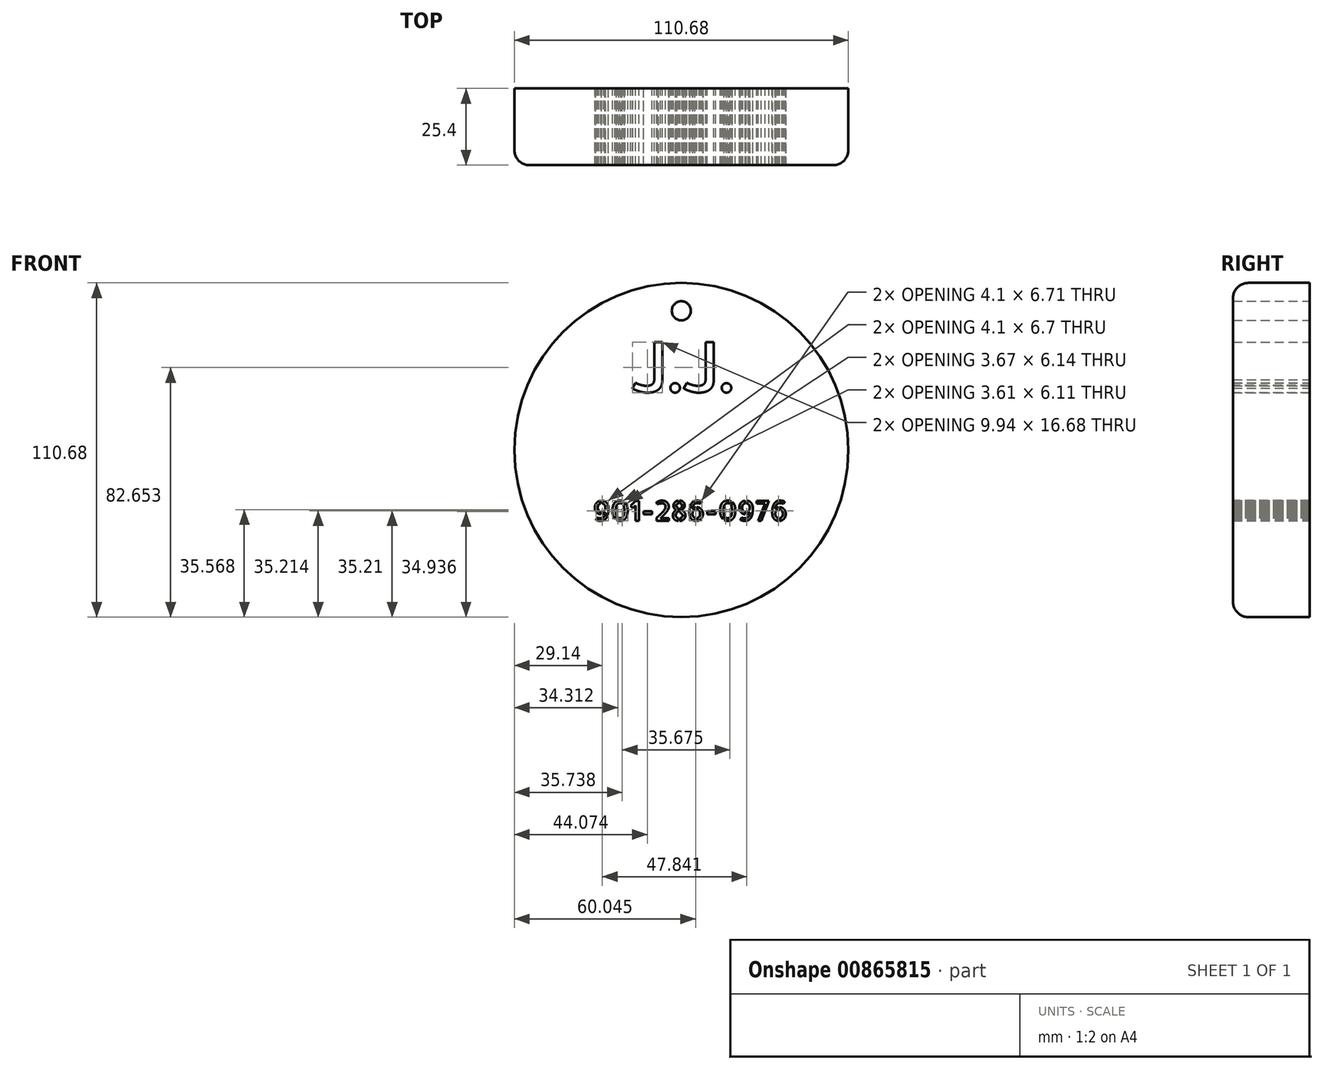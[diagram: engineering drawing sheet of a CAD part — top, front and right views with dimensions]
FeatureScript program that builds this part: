
annotation { "Feature Type Name" : "Feature", "Feature Type Description" : "" }
export const myFeature = defineFeature(function(context is Context, id is Id, definition is map)
    precondition{}
    {
        {
            var Q0;
            Q0=qCreatedBy(makeId("Front.planeOp"),FACE);
            var sketch = newSketch(context, id + "F0", { "sketchPlane" : qUnion([Q0])});
            skCircle(sketch, "E0", {"center": v(0, 0) * mm, "radius": 55.34 * mm});
            skText(sketch, "E1", { "text": "J.J.", "fontName": "AllertaStencil-Regular.ttf"});
            skText(sketch, "E2", { "text": "901-286-0976", "fontName": "AllertaStencil-Regular.ttf"});
            const initialGuessF0  = {"E1": [-0.01681, 0.01908, 1, 0, 0.01625], "E2": [-0.02928, -0.02343, 1, 0, 0.00661]};
            skSetInitialGuess(sketch, initialGuessF0);
            skSolve(sketch);
        }
        {
            var Q0;
            Q0 = qSketchRegion(id + "F0", true);
            var Q1;
            Q1=makeQuery(id+"F0.imprint","IMPRINT",FACE,{"disambiguationData":[TD([[makeQuery(id+"F0.imprint","IMPRINT",EDGE,{"derivedFrom":sQuery(id+"F0.wireOp",EDGE,"E0")}),1.0]])]});
            extrude(context, id + "F1", {"entities" : qUnion([Q0, Q1]), "depth" : 25.4 * mm, "offsetDistance" : 25.4 * mm});
        }
        {
            var Q0;
            Q0=qCreatedBy(makeId("Front.planeOp"),FACE);
            var sketch = newSketch(context, id + "F2", { "sketchPlane" : qUnion([Q0])});
            skPoint(sketch, "E3", {"position": v(0, 46.1) * mm});
            skSolve(sketch);
        }
        {
            var Q0;
            Q0=sQuery(id+"F2.wireOp",VERTEX,"E3");
            var Q1;
            Q1=makeQuery(id+"F1.opExtrude","SWEPT_BODY",BODY,{"disambiguationData":[OSD([sQuery(id+"F0.wireOp",EDGE,"E0"),sQuery(id+"F0.wireOp",EDGE,"E1.sketch_text.stroke-0"),sQuery(id+"F0.wireOp",EDGE,"E1.sketch_text.stroke-1"),sQuery(id+"F0.wireOp",EDGE,"E1.sketch_text.stroke-2"),sQuery(id+"F0.wireOp",EDGE,"E1.sketch_text.stroke-3"),sQuery(id+"F0.wireOp",EDGE,"E1.sketch_text.stroke-4"),sQuery(id+"F0.wireOp",EDGE,"E1.sketch_text.stroke-5"),sQuery(id+"F0.wireOp",EDGE,"E1.sketch_text.stroke-6"),sQuery(id+"F0.wireOp",EDGE,"E1.sketch_text.stroke-7"),sQuery(id+"F0.wireOp",EDGE,"E1.sketch_text.stroke-8"),sQuery(id+"F0.wireOp",EDGE,"E1.sketch_text.stroke-9"),sQuery(id+"F0.wireOp",EDGE,"E1.sketch_text.stroke-10"),sQuery(id+"F0.wireOp",EDGE,"E1.sketch_text.stroke-11"),sQuery(id+"F0.wireOp",EDGE,"E1.sketch_text.stroke-12"),sQuery(id+"F0.wireOp",EDGE,"E1.sketch_text.stroke-13"),sQuery(id+"F0.wireOp",EDGE,"E1.sketch_text.stroke-14"),sQuery(id+"F0.wireOp",EDGE,"E1.sketch_text.stroke-15"),sQuery(id+"F0.wireOp",EDGE,"E1.sketch_text.stroke-16"),sQuery(id+"F0.wireOp",EDGE,"E1.sketch_text.stroke-17"),sQuery(id+"F0.wireOp",EDGE,"E1.sketch_text.stroke-18"),sQuery(id+"F0.wireOp",EDGE,"E1.sketch_text.stroke-19"),sQuery(id+"F0.wireOp",EDGE,"E1.sketch_text.stroke-20"),sQuery(id+"F0.wireOp",EDGE,"E1.sketch_text.stroke-21"),sQuery(id+"F0.wireOp",EDGE,"E1.sketch_text.stroke-22"),sQuery(id+"F0.wireOp",EDGE,"E1.sketch_text.stroke-23"),sQuery(id+"F0.wireOp",EDGE,"E1.sketch_text.stroke-24"),sQuery(id+"F0.wireOp",EDGE,"E1.sketch_text.stroke-25"),sQuery(id+"F0.wireOp",EDGE,"E1.sketch_text.stroke-26"),sQuery(id+"F0.wireOp",EDGE,"E1.sketch_text.stroke-27"),sQuery(id+"F0.wireOp",EDGE,"E1.sketch_text.stroke-28"),sQuery(id+"F0.wireOp",EDGE,"E1.sketch_text.stroke-29"),sQuery(id+"F0.wireOp",EDGE,"E1.sketch_text.stroke-30"),sQuery(id+"F0.wireOp",EDGE,"E1.sketch_text.stroke-31"),sQuery(id+"F0.wireOp",EDGE,"E1.sketch_text.stroke-32"),sQuery(id+"F0.wireOp",EDGE,"E1.sketch_text.stroke-33"),sQuery(id+"F0.wireOp",EDGE,"E1.sketch_text.stroke-34"),sQuery(id+"F0.wireOp",EDGE,"E1.sketch_text.stroke-35"),sQuery(id+"F0.wireOp",EDGE,"E1.sketch_text.stroke-36"),sQuery(id+"F0.wireOp",EDGE,"E1.sketch_text.stroke-37"),sQuery(id+"F0.wireOp",EDGE,"E1.sketch_text.stroke-38"),sQuery(id+"F0.wireOp",EDGE,"E1.sketch_text.stroke-39"),sQuery(id+"F0.wireOp",EDGE,"E1.sketch_text.stroke-40"),sQuery(id+"F0.wireOp",EDGE,"E1.sketch_text.stroke-41"),sQuery(id+"F0.wireOp",EDGE,"E1.sketch_text.stroke-42"),sQuery(id+"F0.wireOp",EDGE,"E1.sketch_text.stroke-43"),sQuery(id+"F0.wireOp",EDGE,"E1.sketch_text.stroke-44"),sQuery(id+"F0.wireOp",EDGE,"E1.sketch_text.stroke-45"),sQuery(id+"F0.wireOp",EDGE,"E1.sketch_text.stroke-46"),sQuery(id+"F0.wireOp",EDGE,"E1.sketch_text.stroke-47"),sQuery(id+"F0.wireOp",EDGE,"E1.sketch_text.stroke-48"),sQuery(id+"F0.wireOp",EDGE,"E1.sketch_text.stroke-49"),sQuery(id+"F0.wireOp",EDGE,"E1.sketch_text.stroke-50"),sQuery(id+"F0.wireOp",EDGE,"E1.sketch_text.stroke-51"),sQuery(id+"F0.wireOp",EDGE,"E2.sketch_text.stroke-0"),sQuery(id+"F0.wireOp",EDGE,"E2.sketch_text.stroke-1"),sQuery(id+"F0.wireOp",EDGE,"E2.sketch_text.stroke-2"),sQuery(id+"F0.wireOp",EDGE,"E2.sketch_text.stroke-3"),sQuery(id+"F0.wireOp",EDGE,"E2.sketch_text.stroke-4"),sQuery(id+"F0.wireOp",EDGE,"E2.sketch_text.stroke-5"),sQuery(id+"F0.wireOp",EDGE,"E2.sketch_text.stroke-6"),sQuery(id+"F0.wireOp",EDGE,"E2.sketch_text.stroke-7"),sQuery(id+"F0.wireOp",EDGE,"E2.sketch_text.stroke-8"),sQuery(id+"F0.wireOp",EDGE,"E2.sketch_text.stroke-9"),sQuery(id+"F0.wireOp",EDGE,"E2.sketch_text.stroke-10"),sQuery(id+"F0.wireOp",EDGE,"E2.sketch_text.stroke-11"),sQuery(id+"F0.wireOp",EDGE,"E2.sketch_text.stroke-12"),sQuery(id+"F0.wireOp",EDGE,"E2.sketch_text.stroke-13"),sQuery(id+"F0.wireOp",EDGE,"E2.sketch_text.stroke-14"),sQuery(id+"F0.wireOp",EDGE,"E2.sketch_text.stroke-15"),sQuery(id+"F0.wireOp",EDGE,"E2.sketch_text.stroke-16"),sQuery(id+"F0.wireOp",EDGE,"E2.sketch_text.stroke-17"),sQuery(id+"F0.wireOp",EDGE,"E2.sketch_text.stroke-18"),sQuery(id+"F0.wireOp",EDGE,"E2.sketch_text.stroke-19"),sQuery(id+"F0.wireOp",EDGE,"E2.sketch_text.stroke-20"),sQuery(id+"F0.wireOp",EDGE,"E2.sketch_text.stroke-21"),sQuery(id+"F0.wireOp",EDGE,"E2.sketch_text.stroke-22"),sQuery(id+"F0.wireOp",EDGE,"E2.sketch_text.stroke-23"),sQuery(id+"F0.wireOp",EDGE,"E2.sketch_text.stroke-24"),sQuery(id+"F0.wireOp",EDGE,"E2.sketch_text.stroke-25"),sQuery(id+"F0.wireOp",EDGE,"E2.sketch_text.stroke-26"),sQuery(id+"F0.wireOp",EDGE,"E2.sketch_text.stroke-27"),sQuery(id+"F0.wireOp",EDGE,"E2.sketch_text.stroke-28"),sQuery(id+"F0.wireOp",EDGE,"E2.sketch_text.stroke-29"),sQuery(id+"F0.wireOp",EDGE,"E2.sketch_text.stroke-30"),sQuery(id+"F0.wireOp",EDGE,"E2.sketch_text.stroke-31"),sQuery(id+"F0.wireOp",EDGE,"E2.sketch_text.stroke-32"),sQuery(id+"F0.wireOp",EDGE,"E2.sketch_text.stroke-33"),sQuery(id+"F0.wireOp",EDGE,"E2.sketch_text.stroke-34"),sQuery(id+"F0.wireOp",EDGE,"E2.sketch_text.stroke-35"),sQuery(id+"F0.wireOp",EDGE,"E2.sketch_text.stroke-36"),sQuery(id+"F0.wireOp",EDGE,"E2.sketch_text.stroke-37"),sQuery(id+"F0.wireOp",EDGE,"E2.sketch_text.stroke-38"),sQuery(id+"F0.wireOp",EDGE,"E2.sketch_text.stroke-39"),sQuery(id+"F0.wireOp",EDGE,"E2.sketch_text.stroke-40"),sQuery(id+"F0.wireOp",EDGE,"E2.sketch_text.stroke-41"),sQuery(id+"F0.wireOp",EDGE,"E2.sketch_text.stroke-42"),sQuery(id+"F0.wireOp",EDGE,"E2.sketch_text.stroke-43"),sQuery(id+"F0.wireOp",EDGE,"E2.sketch_text.stroke-44"),sQuery(id+"F0.wireOp",EDGE,"E2.sketch_text.stroke-45"),sQuery(id+"F0.wireOp",EDGE,"E2.sketch_text.stroke-46"),sQuery(id+"F0.wireOp",EDGE,"E2.sketch_text.stroke-47"),sQuery(id+"F0.wireOp",EDGE,"E2.sketch_text.stroke-48"),sQuery(id+"F0.wireOp",EDGE,"E2.sketch_text.stroke-49"),sQuery(id+"F0.wireOp",EDGE,"E2.sketch_text.stroke-50"),sQuery(id+"F0.wireOp",EDGE,"E2.sketch_text.stroke-51"),sQuery(id+"F0.wireOp",EDGE,"E2.sketch_text.stroke-52"),sQuery(id+"F0.wireOp",EDGE,"E2.sketch_text.stroke-53"),sQuery(id+"F0.wireOp",EDGE,"E2.sketch_text.stroke-54"),sQuery(id+"F0.wireOp",EDGE,"E2.sketch_text.stroke-55"),sQuery(id+"F0.wireOp",EDGE,"E2.sketch_text.stroke-56"),sQuery(id+"F0.wireOp",EDGE,"E2.sketch_text.stroke-57"),sQuery(id+"F0.wireOp",EDGE,"E2.sketch_text.stroke-58"),sQuery(id+"F0.wireOp",EDGE,"E2.sketch_text.stroke-59"),sQuery(id+"F0.wireOp",EDGE,"E2.sketch_text.stroke-60"),sQuery(id+"F0.wireOp",EDGE,"E2.sketch_text.stroke-61"),sQuery(id+"F0.wireOp",EDGE,"E2.sketch_text.stroke-62"),sQuery(id+"F0.wireOp",EDGE,"E2.sketch_text.stroke-63"),sQuery(id+"F0.wireOp",EDGE,"E2.sketch_text.stroke-64"),sQuery(id+"F0.wireOp",EDGE,"E2.sketch_text.stroke-65"),sQuery(id+"F0.wireOp",EDGE,"E2.sketch_text.stroke-66"),sQuery(id+"F0.wireOp",EDGE,"E2.sketch_text.stroke-67"),sQuery(id+"F0.wireOp",EDGE,"E2.sketch_text.stroke-68"),sQuery(id+"F0.wireOp",EDGE,"E2.sketch_text.stroke-69"),sQuery(id+"F0.wireOp",EDGE,"E2.sketch_text.stroke-70"),sQuery(id+"F0.wireOp",EDGE,"E2.sketch_text.stroke-71"),sQuery(id+"F0.wireOp",EDGE,"E2.sketch_text.stroke-72"),sQuery(id+"F0.wireOp",EDGE,"E2.sketch_text.stroke-73"),sQuery(id+"F0.wireOp",EDGE,"E2.sketch_text.stroke-74"),sQuery(id+"F0.wireOp",EDGE,"E2.sketch_text.stroke-75"),sQuery(id+"F0.wireOp",EDGE,"E2.sketch_text.stroke-76"),sQuery(id+"F0.wireOp",EDGE,"E2.sketch_text.stroke-77"),sQuery(id+"F0.wireOp",EDGE,"E2.sketch_text.stroke-78"),sQuery(id+"F0.wireOp",EDGE,"E2.sketch_text.stroke-79"),sQuery(id+"F0.wireOp",EDGE,"E2.sketch_text.stroke-80"),sQuery(id+"F0.wireOp",EDGE,"E2.sketch_text.stroke-81"),sQuery(id+"F0.wireOp",EDGE,"E2.sketch_text.stroke-82"),sQuery(id+"F0.wireOp",EDGE,"E2.sketch_text.stroke-83"),sQuery(id+"F0.wireOp",EDGE,"E2.sketch_text.stroke-84"),sQuery(id+"F0.wireOp",EDGE,"E2.sketch_text.stroke-85"),sQuery(id+"F0.wireOp",EDGE,"E2.sketch_text.stroke-86"),sQuery(id+"F0.wireOp",EDGE,"E2.sketch_text.stroke-87"),sQuery(id+"F0.wireOp",EDGE,"E2.sketch_text.stroke-88"),sQuery(id+"F0.wireOp",EDGE,"E2.sketch_text.stroke-89"),sQuery(id+"F0.wireOp",EDGE,"E2.sketch_text.stroke-90"),sQuery(id+"F0.wireOp",EDGE,"E2.sketch_text.stroke-91"),sQuery(id+"F0.wireOp",EDGE,"E2.sketch_text.stroke-92"),sQuery(id+"F0.wireOp",EDGE,"E2.sketch_text.stroke-93"),sQuery(id+"F0.wireOp",EDGE,"E2.sketch_text.stroke-94"),sQuery(id+"F0.wireOp",EDGE,"E2.sketch_text.stroke-95"),sQuery(id+"F0.wireOp",EDGE,"E2.sketch_text.stroke-96"),sQuery(id+"F0.wireOp",EDGE,"E2.sketch_text.stroke-97"),sQuery(id+"F0.wireOp",EDGE,"E2.sketch_text.stroke-98"),sQuery(id+"F0.wireOp",EDGE,"E2.sketch_text.stroke-99"),sQuery(id+"F0.wireOp",EDGE,"E2.sketch_text.stroke-100"),sQuery(id+"F0.wireOp",EDGE,"E2.sketch_text.stroke-101"),sQuery(id+"F0.wireOp",EDGE,"E2.sketch_text.stroke-102"),sQuery(id+"F0.wireOp",EDGE,"E2.sketch_text.stroke-103"),sQuery(id+"F0.wireOp",EDGE,"E2.sketch_text.stroke-104"),sQuery(id+"F0.wireOp",EDGE,"E2.sketch_text.stroke-105"),sQuery(id+"F0.wireOp",EDGE,"E2.sketch_text.stroke-106"),sQuery(id+"F0.wireOp",EDGE,"E2.sketch_text.stroke-107"),sQuery(id+"F0.wireOp",EDGE,"E2.sketch_text.stroke-108"),sQuery(id+"F0.wireOp",EDGE,"E2.sketch_text.stroke-109"),sQuery(id+"F0.wireOp",EDGE,"E2.sketch_text.stroke-110"),sQuery(id+"F0.wireOp",EDGE,"E2.sketch_text.stroke-111"),sQuery(id+"F0.wireOp",EDGE,"E2.sketch_text.stroke-112"),sQuery(id+"F0.wireOp",EDGE,"E2.sketch_text.stroke-113"),sQuery(id+"F0.wireOp",EDGE,"E2.sketch_text.stroke-114"),sQuery(id+"F0.wireOp",EDGE,"E2.sketch_text.stroke-115"),sQuery(id+"F0.wireOp",EDGE,"E2.sketch_text.stroke-116"),sQuery(id+"F0.wireOp",EDGE,"E2.sketch_text.stroke-117"),sQuery(id+"F0.wireOp",EDGE,"E2.sketch_text.stroke-118"),sQuery(id+"F0.wireOp",EDGE,"E2.sketch_text.stroke-119"),sQuery(id+"F0.wireOp",EDGE,"E2.sketch_text.stroke-120"),sQuery(id+"F0.wireOp",EDGE,"E2.sketch_text.stroke-121"),sQuery(id+"F0.wireOp",EDGE,"E2.sketch_text.stroke-122"),sQuery(id+"F0.wireOp",EDGE,"E2.sketch_text.stroke-123"),sQuery(id+"F0.wireOp",EDGE,"E2.sketch_text.stroke-124"),sQuery(id+"F0.wireOp",EDGE,"E2.sketch_text.stroke-125"),sQuery(id+"F0.wireOp",EDGE,"E2.sketch_text.stroke-126"),sQuery(id+"F0.wireOp",EDGE,"E2.sketch_text.stroke-127"),sQuery(id+"F0.wireOp",EDGE,"E2.sketch_text.stroke-128"),sQuery(id+"F0.wireOp",EDGE,"E2.sketch_text.stroke-129"),sQuery(id+"F0.wireOp",EDGE,"E2.sketch_text.stroke-130"),sQuery(id+"F0.wireOp",EDGE,"E2.sketch_text.stroke-131"),sQuery(id+"F0.wireOp",EDGE,"E2.sketch_text.stroke-132"),sQuery(id+"F0.wireOp",EDGE,"E2.sketch_text.stroke-133"),sQuery(id+"F0.wireOp",EDGE,"E2.sketch_text.stroke-134"),sQuery(id+"F0.wireOp",EDGE,"E2.sketch_text.stroke-135"),sQuery(id+"F0.wireOp",EDGE,"E2.sketch_text.stroke-136"),sQuery(id+"F0.wireOp",EDGE,"E2.sketch_text.stroke-137"),sQuery(id+"F0.wireOp",EDGE,"E2.sketch_text.stroke-138"),sQuery(id+"F0.wireOp",EDGE,"E2.sketch_text.stroke-139"),sQuery(id+"F0.wireOp",EDGE,"E2.sketch_text.stroke-140"),sQuery(id+"F0.wireOp",EDGE,"E2.sketch_text.stroke-141"),sQuery(id+"F0.wireOp",EDGE,"E2.sketch_text.stroke-142"),sQuery(id+"F0.wireOp",EDGE,"E2.sketch_text.stroke-143"),sQuery(id+"F0.wireOp",EDGE,"E2.sketch_text.stroke-144"),sQuery(id+"F0.wireOp",EDGE,"E2.sketch_text.stroke-145"),sQuery(id+"F0.wireOp",EDGE,"E2.sketch_text.stroke-146"),sQuery(id+"F0.wireOp",EDGE,"E2.sketch_text.stroke-147"),sQuery(id+"F0.wireOp",EDGE,"E2.sketch_text.stroke-148"),sQuery(id+"F0.wireOp",EDGE,"E2.sketch_text.stroke-149"),sQuery(id+"F0.wireOp",EDGE,"E2.sketch_text.stroke-150"),sQuery(id+"F0.wireOp",EDGE,"E2.sketch_text.stroke-151"),sQuery(id+"F0.wireOp",EDGE,"E2.sketch_text.stroke-152"),sQuery(id+"F0.wireOp",EDGE,"E2.sketch_text.stroke-153"),sQuery(id+"F0.wireOp",EDGE,"E2.sketch_text.stroke-154"),sQuery(id+"F0.wireOp",EDGE,"E2.sketch_text.stroke-155"),sQuery(id+"F0.wireOp",EDGE,"E2.sketch_text.stroke-156"),sQuery(id+"F0.wireOp",EDGE,"E2.sketch_text.stroke-157"),sQuery(id+"F0.wireOp",EDGE,"E2.sketch_text.stroke-158"),sQuery(id+"F0.wireOp",EDGE,"E2.sketch_text.stroke-159"),sQuery(id+"F0.wireOp",EDGE,"E2.sketch_text.stroke-160"),sQuery(id+"F0.wireOp",EDGE,"E2.sketch_text.stroke-161"),sQuery(id+"F0.wireOp",EDGE,"E2.sketch_text.stroke-162"),sQuery(id+"F0.wireOp",EDGE,"E2.sketch_text.stroke-163"),sQuery(id+"F0.wireOp",EDGE,"E2.sketch_text.stroke-164"),sQuery(id+"F0.wireOp",EDGE,"E2.sketch_text.stroke-165"),sQuery(id+"F0.wireOp",EDGE,"E2.sketch_text.stroke-166"),sQuery(id+"F0.wireOp",EDGE,"E2.sketch_text.stroke-167"),sQuery(id+"F0.wireOp",EDGE,"E2.sketch_text.stroke-168"),sQuery(id+"F0.wireOp",EDGE,"E2.sketch_text.stroke-169"),sQuery(id+"F0.wireOp",EDGE,"E2.sketch_text.stroke-170"),sQuery(id+"F0.wireOp",EDGE,"E2.sketch_text.stroke-171"),sQuery(id+"F0.wireOp",EDGE,"E2.sketch_text.stroke-172"),sQuery(id+"F0.wireOp",EDGE,"E2.sketch_text.stroke-173"),sQuery(id+"F0.wireOp",EDGE,"E2.sketch_text.stroke-174"),sQuery(id+"F0.wireOp",EDGE,"E2.sketch_text.stroke-175"),sQuery(id+"F0.wireOp",EDGE,"E2.sketch_text.stroke-176"),sQuery(id+"F0.wireOp",EDGE,"E2.sketch_text.stroke-177"),sQuery(id+"F0.wireOp",EDGE,"E2.sketch_text.stroke-178"),sQuery(id+"F0.wireOp",EDGE,"E2.sketch_text.stroke-179"),sQuery(id+"F0.wireOp",EDGE,"E2.sketch_text.stroke-180"),sQuery(id+"F0.wireOp",EDGE,"E2.sketch_text.stroke-181"),sQuery(id+"F0.wireOp",EDGE,"E2.sketch_text.stroke-182"),sQuery(id+"F0.wireOp",EDGE,"E2.sketch_text.stroke-183"),sQuery(id+"F0.wireOp",EDGE,"E2.sketch_text.stroke-184"),sQuery(id+"F0.wireOp",EDGE,"E2.sketch_text.stroke-185"),sQuery(id+"F0.wireOp",EDGE,"E2.sketch_text.stroke-186"),sQuery(id+"F0.wireOp",EDGE,"E2.sketch_text.stroke-187"),sQuery(id+"F0.wireOp",EDGE,"E2.sketch_text.stroke-188"),sQuery(id+"F0.wireOp",EDGE,"E2.sketch_text.stroke-189"),sQuery(id+"F0.wireOp",EDGE,"E2.sketch_text.stroke-190"),sQuery(id+"F0.wireOp",EDGE,"E2.sketch_text.stroke-191"),sQuery(id+"F0.wireOp",EDGE,"E2.sketch_text.stroke-192"),sQuery(id+"F0.wireOp",EDGE,"E2.sketch_text.stroke-193"),sQuery(id+"F0.wireOp",EDGE,"E2.sketch_text.stroke-194"),sQuery(id+"F0.wireOp",EDGE,"E2.sketch_text.stroke-195"),sQuery(id+"F0.wireOp",EDGE,"E2.sketch_text.stroke-196"),sQuery(id+"F0.wireOp",EDGE,"E2.sketch_text.stroke-197"),sQuery(id+"F0.wireOp",EDGE,"E2.sketch_text.stroke-198"),sQuery(id+"F0.wireOp",EDGE,"E2.sketch_text.stroke-199"),sQuery(id+"F0.wireOp",EDGE,"E2.sketch_text.stroke-200"),sQuery(id+"F0.wireOp",EDGE,"E2.sketch_text.stroke-201"),sQuery(id+"F0.wireOp",EDGE,"E2.sketch_text.stroke-202"),sQuery(id+"F0.wireOp",EDGE,"E2.sketch_text.stroke-203"),sQuery(id+"F0.wireOp",EDGE,"E2.sketch_text.stroke-204"),sQuery(id+"F0.wireOp",EDGE,"E2.sketch_text.stroke-205"),sQuery(id+"F0.wireOp",EDGE,"E2.sketch_text.stroke-206"),sQuery(id+"F0.wireOp",EDGE,"E2.sketch_text.stroke-207"),sQuery(id+"F0.wireOp",EDGE,"E2.sketch_text.stroke-208"),sQuery(id+"F0.wireOp",EDGE,"E2.sketch_text.stroke-209"),sQuery(id+"F0.wireOp",EDGE,"E2.sketch_text.stroke-210"),sQuery(id+"F0.wireOp",EDGE,"E2.sketch_text.stroke-211"),sQuery(id+"F0.wireOp",EDGE,"E2.sketch_text.stroke-212"),sQuery(id+"F0.wireOp",EDGE,"E2.sketch_text.stroke-213"),sQuery(id+"F0.wireOp",EDGE,"E2.sketch_text.stroke-214"),sQuery(id+"F0.wireOp",EDGE,"E2.sketch_text.stroke-215"),sQuery(id+"F0.wireOp",EDGE,"E2.sketch_text.stroke-216"),sQuery(id+"F0.wireOp",EDGE,"E2.sketch_text.stroke-217"),sQuery(id+"F0.wireOp",EDGE,"E2.sketch_text.stroke-218"),sQuery(id+"F0.wireOp",EDGE,"E2.sketch_text.stroke-219"),sQuery(id+"F0.wireOp",EDGE,"E2.sketch_text.stroke-220"),sQuery(id+"F0.wireOp",EDGE,"E2.sketch_text.stroke-221"),sQuery(id+"F0.wireOp",EDGE,"E2.sketch_text.stroke-222"),sQuery(id+"F0.wireOp",EDGE,"E2.sketch_text.stroke-223"),sQuery(id+"F0.wireOp",EDGE,"E2.sketch_text.stroke-224"),sQuery(id+"F0.wireOp",EDGE,"E2.sketch_text.stroke-225"),sQuery(id+"F0.wireOp",EDGE,"E2.sketch_text.stroke-226"),sQuery(id+"F0.wireOp",EDGE,"E2.sketch_text.stroke-227"),sQuery(id+"F0.wireOp",EDGE,"E2.sketch_text.stroke-228"),sQuery(id+"F0.wireOp",EDGE,"E2.sketch_text.stroke-229"),sQuery(id+"F0.wireOp",EDGE,"E2.sketch_text.stroke-230"),sQuery(id+"F0.wireOp",EDGE,"E2.sketch_text.stroke-231"),sQuery(id+"F0.wireOp",EDGE,"E2.sketch_text.stroke-232"),sQuery(id+"F0.wireOp",EDGE,"E2.sketch_text.stroke-233"),sQuery(id+"F0.wireOp",EDGE,"E2.sketch_text.stroke-234"),sQuery(id+"F0.wireOp",EDGE,"E2.sketch_text.stroke-235"),sQuery(id+"F0.wireOp",EDGE,"E2.sketch_text.stroke-236"),sQuery(id+"F0.wireOp",EDGE,"E2.sketch_text.stroke-237"),sQuery(id+"F0.wireOp",EDGE,"E2.sketch_text.stroke-238"),sQuery(id+"F0.wireOp",EDGE,"E2.sketch_text.stroke-239"),sQuery(id+"F0.wireOp",EDGE,"E2.sketch_text.stroke-240"),sQuery(id+"F0.wireOp",EDGE,"E2.sketch_text.stroke-241"),sQuery(id+"F0.wireOp",EDGE,"E2.sketch_text.stroke-242"),sQuery(id+"F0.wireOp",EDGE,"E2.sketch_text.stroke-243"),sQuery(id+"F0.wireOp",EDGE,"E2.sketch_text.stroke-244"),sQuery(id+"F0.wireOp",EDGE,"E2.sketch_text.stroke-245"),sQuery(id+"F0.wireOp",EDGE,"E2.sketch_text.stroke-246"),sQuery(id+"F0.wireOp",EDGE,"E2.sketch_text.stroke-247"),sQuery(id+"F0.wireOp",EDGE,"E2.sketch_text.stroke-248"),sQuery(id+"F0.wireOp",EDGE,"E2.sketch_text.stroke-249"),sQuery(id+"F0.wireOp",EDGE,"E2.sketch_text.stroke-250"),sQuery(id+"F0.wireOp",EDGE,"E2.sketch_text.stroke-251"),sQuery(id+"F0.wireOp",EDGE,"E2.sketch_text.stroke-252"),sQuery(id+"F0.wireOp",EDGE,"E2.sketch_text.stroke-253"),sQuery(id+"F0.wireOp",EDGE,"E2.sketch_text.stroke-254"),sQuery(id+"F0.wireOp",EDGE,"E2.sketch_text.stroke-255"),sQuery(id+"F0.wireOp",EDGE,"E2.sketch_text.stroke-256"),sQuery(id+"F0.wireOp",EDGE,"E2.sketch_text.stroke-257"),sQuery(id+"F0.wireOp",EDGE,"E2.sketch_text.stroke-258"),sQuery(id+"F0.wireOp",EDGE,"E2.sketch_text.stroke-259"),sQuery(id+"F0.wireOp",EDGE,"E2.sketch_text.stroke-260"),sQuery(id+"F0.wireOp",EDGE,"E2.sketch_text.stroke-261"),sQuery(id+"F0.wireOp",EDGE,"E2.sketch_text.stroke-262"),sQuery(id+"F0.wireOp",EDGE,"E2.sketch_text.stroke-263"),sQuery(id+"F0.wireOp",EDGE,"E2.sketch_text.stroke-264"),sQuery(id+"F0.wireOp",EDGE,"E2.sketch_text.stroke-265"),sQuery(id+"F0.wireOp",EDGE,"E2.sketch_text.stroke-266"),sQuery(id+"F0.wireOp",EDGE,"E2.sketch_text.stroke-267"),sQuery(id+"F0.wireOp",EDGE,"E2.sketch_text.stroke-268"),sQuery(id+"F0.wireOp",EDGE,"E2.sketch_text.stroke-269"),sQuery(id+"F0.wireOp",EDGE,"E2.sketch_text.stroke-270"),sQuery(id+"F0.wireOp",EDGE,"E2.sketch_text.stroke-271"),sQuery(id+"F0.wireOp",EDGE,"E2.sketch_text.stroke-272"),sQuery(id+"F0.wireOp",EDGE,"E2.sketch_text.stroke-273"),sQuery(id+"F0.wireOp",EDGE,"E2.sketch_text.stroke-274"),sQuery(id+"F0.wireOp",EDGE,"E2.sketch_text.stroke-275"),sQuery(id+"F0.wireOp",EDGE,"E2.sketch_text.stroke-276"),sQuery(id+"F0.wireOp",EDGE,"E2.sketch_text.stroke-277"),sQuery(id+"F0.wireOp",EDGE,"E2.sketch_text.stroke-278"),sQuery(id+"F0.wireOp",EDGE,"E2.sketch_text.stroke-279"),sQuery(id+"F0.wireOp",EDGE,"E2.sketch_text.stroke-280"),sQuery(id+"F0.wireOp",EDGE,"E2.sketch_text.stroke-281"),sQuery(id+"F0.wireOp",EDGE,"E2.sketch_text.stroke-282"),sQuery(id+"F0.wireOp",EDGE,"E2.sketch_text.stroke-283"),sQuery(id+"F0.wireOp",EDGE,"E2.sketch_text.stroke-284"),sQuery(id+"F0.wireOp",EDGE,"E2.sketch_text.stroke-285"),sQuery(id+"F0.wireOp",EDGE,"E2.sketch_text.stroke-286"),sQuery(id+"F0.wireOp",EDGE,"E2.sketch_text.stroke-287"),sQuery(id+"F0.wireOp",EDGE,"E2.sketch_text.stroke-288"),sQuery(id+"F0.wireOp",EDGE,"E2.sketch_text.stroke-289"),sQuery(id+"F0.wireOp",EDGE,"E2.sketch_text.stroke-290"),sQuery(id+"F0.wireOp",EDGE,"E2.sketch_text.stroke-291"),sQuery(id+"F0.wireOp",EDGE,"E2.sketch_text.stroke-292"),sQuery(id+"F0.wireOp",EDGE,"E2.sketch_text.stroke-293"),sQuery(id+"F0.wireOp",EDGE,"E2.sketch_text.stroke-294"),sQuery(id+"F0.wireOp",EDGE,"E2.sketch_text.stroke-295"),sQuery(id+"F0.wireOp",EDGE,"E2.sketch_text.stroke-296"),sQuery(id+"F0.wireOp",EDGE,"E2.sketch_text.stroke-297"),sQuery(id+"F0.wireOp",EDGE,"E2.sketch_text.stroke-298"),sQuery(id+"F0.wireOp",EDGE,"E2.sketch_text.stroke-299"),sQuery(id+"F0.wireOp",EDGE,"E2.sketch_text.stroke-300"),sQuery(id+"F0.wireOp",EDGE,"E2.sketch_text.stroke-301"),sQuery(id+"F0.wireOp",EDGE,"E2.sketch_text.stroke-302"),sQuery(id+"F0.wireOp",EDGE,"E2.sketch_text.stroke-303"),sQuery(id+"F0.wireOp",EDGE,"E2.sketch_text.stroke-304"),sQuery(id+"F0.wireOp",EDGE,"E2.sketch_text.stroke-305"),sQuery(id+"F0.wireOp",EDGE,"E2.sketch_text.stroke-306"),sQuery(id+"F0.wireOp",EDGE,"E2.sketch_text.stroke-307"),sQuery(id+"F0.wireOp",EDGE,"E2.sketch_text.stroke-308"),sQuery(id+"F0.wireOp",EDGE,"E2.sketch_text.stroke-309"),sQuery(id+"F0.wireOp",EDGE,"E2.sketch_text.stroke-310"),sQuery(id+"F0.wireOp",EDGE,"E2.sketch_text.stroke-311"),sQuery(id+"F0.wireOp",EDGE,"E2.sketch_text.stroke-312"),sQuery(id+"F0.wireOp",EDGE,"E2.sketch_text.stroke-313"),sQuery(id+"F0.wireOp",EDGE,"E2.sketch_text.stroke-314"),sQuery(id+"F0.wireOp",EDGE,"E2.sketch_text.stroke-315"),sQuery(id+"F0.wireOp",EDGE,"E2.sketch_text.stroke-316"),sQuery(id+"F0.wireOp",EDGE,"E2.sketch_text.stroke-317"),sQuery(id+"F0.wireOp",EDGE,"E2.sketch_text.stroke-318"),sQuery(id+"F0.wireOp",EDGE,"E2.sketch_text.stroke-319"),sQuery(id+"F0.wireOp",EDGE,"E2.sketch_text.stroke-320"),sQuery(id+"F0.wireOp",EDGE,"E2.sketch_text.stroke-321"),sQuery(id+"F0.wireOp",EDGE,"E2.sketch_text.stroke-322"),sQuery(id+"F0.wireOp",EDGE,"E2.sketch_text.stroke-323"),sQuery(id+"F0.wireOp",EDGE,"E2.sketch_text.stroke-324"),sQuery(id+"F0.wireOp",EDGE,"E2.sketch_text.stroke-325"),sQuery(id+"F0.wireOp",EDGE,"E2.sketch_text.stroke-326"),sQuery(id+"F0.wireOp",EDGE,"E2.sketch_text.stroke-327"),sQuery(id+"F0.wireOp",EDGE,"E2.sketch_text.stroke-328"),sQuery(id+"F0.wireOp",EDGE,"E2.sketch_text.stroke-329"),sQuery(id+"F0.wireOp",EDGE,"E2.sketch_text.stroke-330"),sQuery(id+"F0.wireOp",EDGE,"E2.sketch_text.stroke-331"),sQuery(id+"F0.wireOp",EDGE,"E2.sketch_text.stroke-332"),sQuery(id+"F0.wireOp",EDGE,"E2.sketch_text.stroke-333"),sQuery(id+"F0.wireOp",EDGE,"E2.sketch_text.stroke-334"),sQuery(id+"F0.wireOp",EDGE,"E2.sketch_text.stroke-335"),sQuery(id+"F0.wireOp",EDGE,"E2.sketch_text.stroke-336"),sQuery(id+"F0.wireOp",EDGE,"E2.sketch_text.stroke-337"),sQuery(id+"F0.wireOp",EDGE,"E2.sketch_text.stroke-338"),sQuery(id+"F0.wireOp",EDGE,"E2.sketch_text.stroke-339"),sQuery(id+"F0.wireOp",EDGE,"E2.sketch_text.stroke-340"),sQuery(id+"F0.wireOp",EDGE,"E2.sketch_text.stroke-341"),sQuery(id+"F0.wireOp",EDGE,"E2.sketch_text.stroke-342"),sQuery(id+"F0.wireOp",EDGE,"E2.sketch_text.stroke-343"),sQuery(id+"F0.wireOp",EDGE,"E2.sketch_text.stroke-344"),sQuery(id+"F0.wireOp",EDGE,"E2.sketch_text.stroke-345"),sQuery(id+"F0.wireOp",EDGE,"E2.sketch_text.stroke-346"),sQuery(id+"F0.wireOp",EDGE,"E2.sketch_text.stroke-347"),sQuery(id+"F0.wireOp",EDGE,"E2.sketch_text.stroke-348"),sQuery(id+"F0.wireOp",EDGE,"E2.sketch_text.stroke-349"),sQuery(id+"F0.wireOp",EDGE,"E2.sketch_text.stroke-350"),sQuery(id+"F0.wireOp",EDGE,"E2.sketch_text.stroke-351"),sQuery(id+"F0.wireOp",EDGE,"E2.sketch_text.stroke-352"),sQuery(id+"F0.wireOp",EDGE,"E2.sketch_text.stroke-353")])]});
            hole(context, id + "F3", {"style" : HoleStyle.SIMPLE, "endStyle" : HoleEndStyle.THROUGH, "oppositeDirection" : true, "holeDiameter" : 6.35 * mm, "majorDiameter" : 6.35 * mm, "isTappedThrough" : true, "tappedDepth" : 12.7 * mm, "tapClearance" : 3, "locations" : qUnion([Q0]), "scope" : qUnion([Q1])});
        }
        {
            var Q0;
            Q0=makeQuery(id+"F1.opExtrude","CAP_EDGE",EDGE,{"disambiguationData":[OSD([sQuery(id+"F0.wireOp",EDGE,"E0")])],"isStart":false});
            fillet(context, id + "F4", {"entities" : qUnion([Q0]), "radius" : 5.08 * mm, "tangentPropagation" : true, "allowEdgeOverflow" : false});
        }
    });
